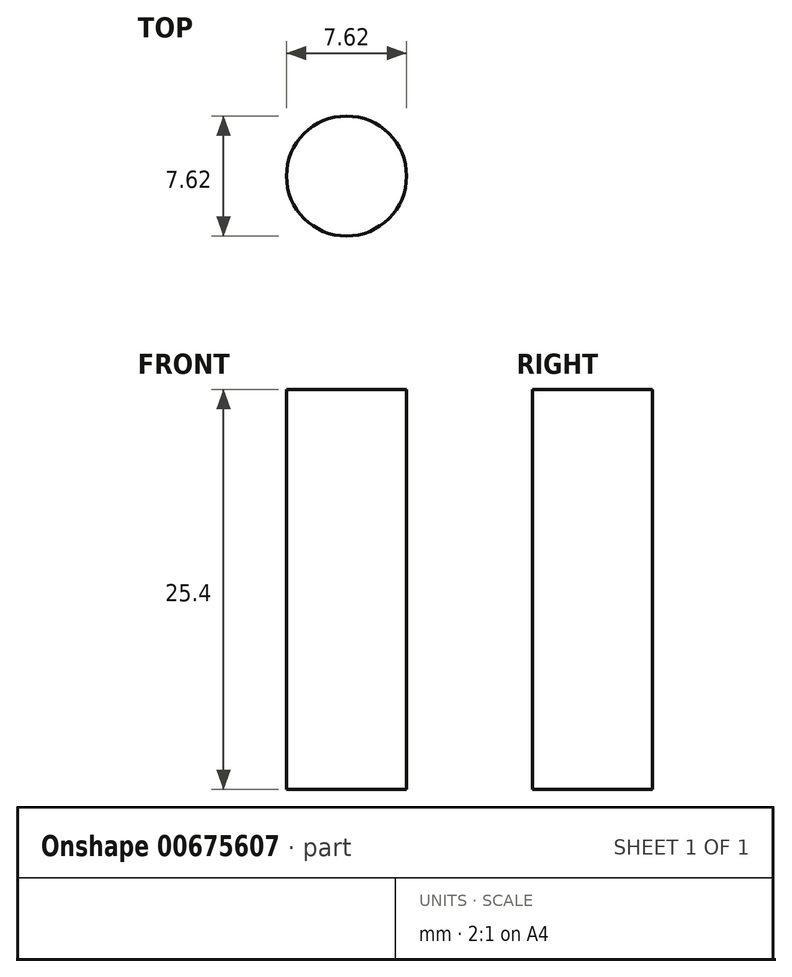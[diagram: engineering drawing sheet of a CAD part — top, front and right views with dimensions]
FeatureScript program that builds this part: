
annotation { "Feature Type Name" : "Feature", "Feature Type Description" : "" }
export const myFeature = defineFeature(function(context is Context, id is Id, definition is map)
    precondition{}
    {
        {
            var Q0;
            Q0=qCreatedBy(makeId("Front.planeOp"),FACE);
            var sketch = newSketch(context, id + "F0", { "sketchPlane" : qUnion([Q0])});
            skLineSegment(sketch, "E0", {"start": v(0, 0) * mm, "end": v(-3.81, 0) * mm});
            skLineSegment(sketch, "E1", {"start": v(-3.81, 0) * mm, "end": v(-3.81, 25.4) * mm});
            skLineSegment(sketch, "E2", {"start": v(-3.81, 25.4) * mm, "end": v(0, 25.4) * mm});
            skLineSegment(sketch, "E3", {"start": v(0, 25.4) * mm, "end": v(0, 0) * mm});
            skSolve(sketch);
        }
        {
            var Q0;
            Q0 = qSketchRegion(id + "F0", true);
            var Q1;
            Q1=sQuery(id+"F0.wireOp",EDGE,"E3");
            revolve(context, id + "F1", {"entities" : qUnion([Q0]), "axis" : qUnion([Q1]), "revolveType" : RevolveType.FULL});
        }
    });
